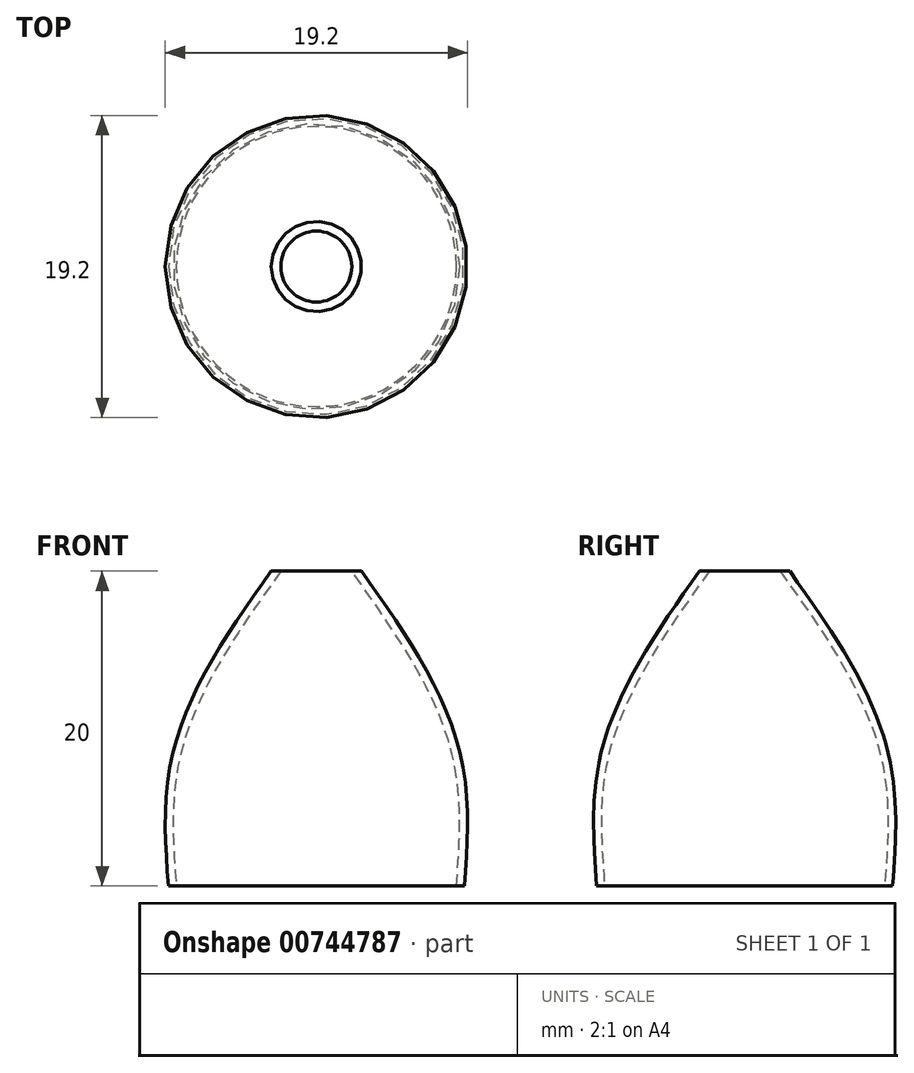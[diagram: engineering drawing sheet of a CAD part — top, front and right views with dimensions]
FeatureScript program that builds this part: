
annotation { "Feature Type Name" : "Feature", "Feature Type Description" : "" }
export const myFeature = defineFeature(function(context is Context, id is Id, definition is map)
    precondition{}
    {
        {
            var Q0;
            Q0=qCreatedBy(makeId("Top.planeOp"),FACE);
            var sketch = newSketch(context, id + "F0", { "sketchPlane" : qUnion([Q0])});
            skCircle(sketch, "E0", {"center": v(0, 0) * mm, "radius": 8.9 * mm});
            skSolve(sketch);
        }
        {
            var Q0;
            Q0=qCreatedBy(makeId("Top.planeOp"),FACE);
            cPlane(context, id + "F1", {"entities" : qUnion([Q0]), "cplaneType" : CPlaneType.OFFSET, "offset" : 7 * mm, "width" : 150 * mm, "height" : 150 * mm});
        }
        {
            var Q0;
            Q0=qCreatedBy(id+"F1.planeOp",FACE);
            cPlane(context, id + "F2", {"entities" : qUnion([Q0]), "cplaneType" : CPlaneType.OFFSET, "offset" : 13 * mm, "width" : 150 * mm, "height" : 150 * mm});
        }
        {
            var Q0;
            Q0=qCreatedBy(id+"F2.planeOp",FACE);
            var sketch = newSketch(context, id + "F3", { "sketchPlane" : qUnion([Q0])});
            skCircle(sketch, "E1", {"center": v(0, 0) * mm, "radius": 2.25 * mm});
            skSolve(sketch);
        }
        {
            var Q0;
            Q0=qCreatedBy(id+"F1.planeOp",FACE);
            var sketch = newSketch(context, id + "F4", { "sketchPlane" : qUnion([Q0])});
            skCircle(sketch, "E2", {"center": v(0, 0) * mm, "radius": 8.9 * mm});
            skSolve(sketch);
        }
        {
            var Q0;
            Q0=qSketchRegion(id+"F0",true);
            var Q1;
            Q1=qSketchRegion(id+"F4",true);
            var Q2;
            Q2=qSketchRegion(id+"F3",true);
            loft(context, id + "F5", {"sheetProfilesArray" : [{ "sheetProfileEntities" : qUnion([Q0]) }, { "sheetProfileEntities" : qUnion([Q1]) }, { "sheetProfileEntities" : qUnion([Q2]) }]});
        }
        {
            var Q0;
            Q0=makeQuery(id+"F5.opLoft","CAP_FACE",FACE,{"disambiguationData":[OSD([makeQuery(id+"F0.imprint","IMPRINT",FACE,{"disambiguationData":[TD([[makeQuery(id+"F0.imprint","IMPRINT",EDGE,{"derivedFrom":sQuery(id+"F0.wireOp",EDGE,"E0")}),1.0]])]})])],"isStart":true});
            var Q1;
            Q1=makeQuery(id+"F5.opLoft","CAP_FACE",FACE,{"disambiguationData":[OSD([makeQuery(id+"F3.imprint","IMPRINT",FACE,{"disambiguationData":[TD([[makeQuery(id+"F3.imprint","IMPRINT",EDGE,{"derivedFrom":sQuery(id+"F3.wireOp",EDGE,"E1")}),1.0]])]})])],"isStart":true});
            shell(context, id + "F6", {"entities" : qUnion([Q0, Q1]), "thickness" : .5 * mm, "oppositeDirection" : true});
        }
    });
